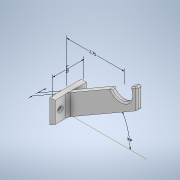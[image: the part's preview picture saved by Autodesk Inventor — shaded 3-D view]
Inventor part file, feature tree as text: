
AUTODESK INVENTOR PART (.ipt)
format: ipt  version: 2021.1 (Build 251245010, 245A)  size: 395,776 bytes
history: native  units: in
note: dims shown in document units (in); Inventor stores cm internally (conversion verified against a paired STEP export)
features: other x5, sketch x5, extrude x4, fillet x4, hole x1
ambient origin geometry x8: Origin, YZ Plane, XZ Plane, XY Plane, X Axis, Y Axis, Z Axis, Center Point
bodies: Solid2 (feature_tree)
feature tree (19):
  other  "Annotations"
  extrude  "Extrusion3"  Depth=0.25in
  extrude  "Extrusion4"  TaperAngle=30.0deg  [1 undecoded]
  sketch  "Sketch7"  dims[d26=1.075in d29=0.25in]
  extrude  "Extrusion5"  Depth=0.25in
  hole  "Hole3"  [1 undecoded]
  fillet  "Fillet3"  [1 undecoded]
  fillet  "Fillet4"  [1 undecoded]
  fillet  "Fillet5"  Radius=0.25in
  fillet  "Fillet6"  Radius=0.25in
  extrude  "Extrusion6"  Depth=0.0625in
  sketch  "Sketch5"  dims[d21=1.0in d22=0.25in]
  sketch  "Sketch6"  dims[d23=1.5in d24=0.0in d25=30.0deg]
  sketch  "Sketch8"  dims[d30=2.75in d31=0.25in d32=0.0in d33=0.0in d34=0.25in d35=0.25in]
  sketch  "Sketch9"  dims[d47=1.5in d48=0.0in d49=0.15in d50=0.75in d51=0.279in d52=0.25in d53=0.5635in d54=1.0in d55=0.8108in d65=0.0625in d66=0.0625in d67=0.0625in d68=0.125in d72=0.05in d73=0.0in d56=0.2085in d57=0.331in d58=1.5in d59=2.3174in d60=30.0deg d69=2.75in d70=0.3005in d71=0.25in]
  other  "Linear Dimension 1"
  other  "Angular Dimension 1"
  other  "Linear Dimension 2"
  other  "Linear Dimension 3"
note: 4 required parameter values undecoded (feature->parameter linkage not recoverable at this tier; creation-order binding heuristic only, values carry confidence <= 0.55)
